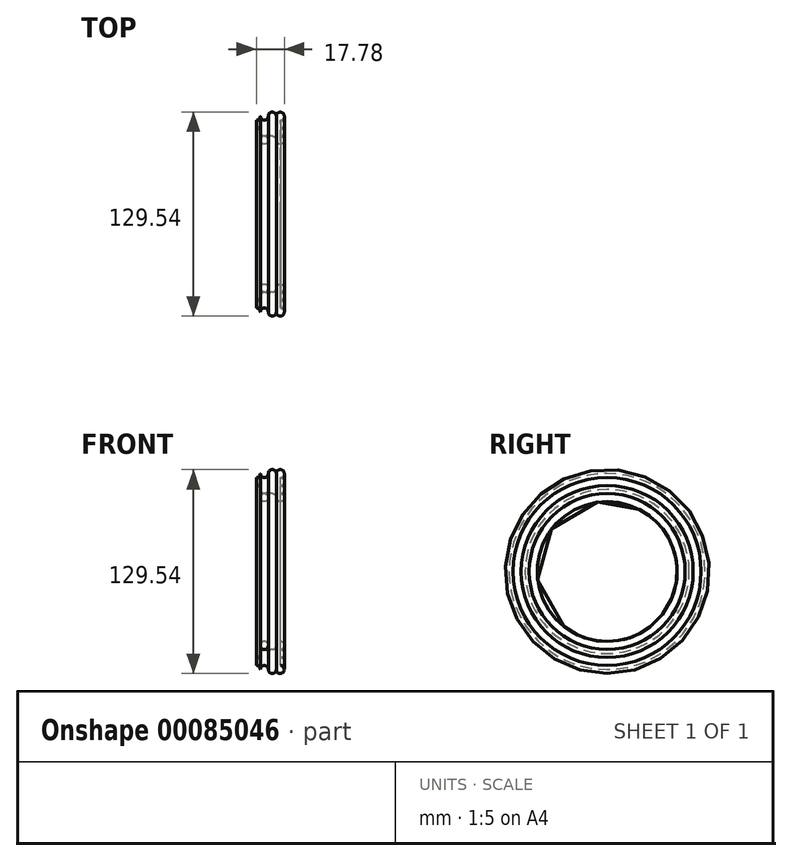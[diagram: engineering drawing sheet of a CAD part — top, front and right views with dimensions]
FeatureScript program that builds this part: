
annotation { "Feature Type Name" : "Feature", "Feature Type Description" : "" }
export const myFeature = defineFeature(function(context is Context, id is Id, definition is map)
    precondition{}
    {
        {
            var Q0;
            Q0=qCreatedBy(makeId("Front.planeOp"),FACE);
            var sketch = newSketch(context, id + "F0", { "sketchPlane" : qUnion([Q0])});
            skLineSegment(sketch, "E0", {"start": v(-20.2, 0) * mm, "end": v(26, 0) * mm, "construction": true});
            skLineSegment(sketch, "E1", {"start": v(-21.51, -21.51) * mm, "end": v(18.59, 18.59) * mm, "construction": true});
            skLineSegment(sketch, "E2", {"start": v(-19.72, 19.72) * mm, "end": v(23.47, -23.47) * mm, "construction": true});
            skCircle(sketch, "E3", {"center": v(-2.54, 2.54) * mm, "radius": 2.54 * mm});
            skCircle(sketch, "E4", {"center": v(2.54, 2.54) * mm, "radius": 2.54 * mm});
            skCircle(sketch, "E5.MirrorC", {"center": v(2.54, -2.54) * mm, "radius": 2.54 * mm});
            skCircle(sketch, "E6.MirrorC", {"center": v(-2.54, -2.54) * mm, "radius": 2.54 * mm});
            skCircle(sketch, "E7", {"center": v(7.62, 7.62) * mm, "radius": 2.54 * mm});
            skCircle(sketch, "E8", {"center": v(7.62, -7.62) * mm, "radius": 2.54 * mm});
            skCircle(sketch, "E9", {"center": v(7.62, -2.54) * mm, "radius": 2.54 * mm});
            skCircle(sketch, "E10", {"center": v(7.62, 2.54) * mm, "radius": 2.54 * mm});
            skCircle(sketch, "E11", {"center": v(2.54, 7.62) * mm, "radius": 2.54 * mm});
            skCircle(sketch, "E12.MirrorC", {"center": v(2.54, -7.62) * mm, "radius": 2.54 * mm});
            skLineSegment(sketch, "E13", {"start": v(0, -13.04) * mm, "end": v(0, 13.76) * mm, "construction": true});
            skCircle(sketch, "E14.MirrorC", {"center": v(-2.54, 7.62) * mm, "radius": 2.54 * mm});
            skCircle(sketch, "E15.MirrorC", {"center": v(-7.62, 7.62) * mm, "radius": 2.54 * mm});
            skCircle(sketch, "E16.MirrorC", {"center": v(-7.62, 2.54) * mm, "radius": 2.54 * mm});
            skCircle(sketch, "E17.MirrorC", {"center": v(-7.62, -2.54) * mm, "radius": 2.54 * mm});
            skCircle(sketch, "E18.MirrorC", {"center": v(-7.62, -7.62) * mm, "radius": 2.54 * mm});
            skCircle(sketch, "E19.MirrorC", {"center": v(-2.54, -7.62) * mm, "radius": 2.54 * mm});
            skLineSegment(sketch, "E20", {"start": v(94.82, -54.61) * mm, "end": v(-108.65, -54.61) * mm, "construction": true});
            skSolve(sketch);
        }
        {
            var Q0;
            {var subQ0=sQuery(id+"F0.wireOp",EDGE,"E8");var subQ1=makeQuery(id+"F0.imprint","INTERSECT",VERTEX,{"derivedFrom":[subQ0,sQuery(id+"F0.wireOp",EDGE,"E9")]});Q0=makeQuery(id+"F0.imprint","IMPRINT",FACE,{"disambiguationData":[TD([[makeQuery(id+"F0.imprint","IMPRINT",EDGE,{"disambiguationData":[TD([[subQ1,-1.0]])],"derivedFrom":subQ0}),1.0]])]});}
            var Q1;
            {var subQ0=sQuery(id+"F0.wireOp",EDGE,"E7");var subQ1=makeQuery(id+"F0.imprint","INTERSECT",VERTEX,{"derivedFrom":[subQ0,sQuery(id+"F0.wireOp",EDGE,"E10")]});Q1=makeQuery(id+"F0.imprint","IMPRINT",FACE,{"disambiguationData":[TD([[makeQuery(id+"F0.imprint","IMPRINT",EDGE,{"disambiguationData":[TD([[subQ1,1.0]])],"derivedFrom":subQ0}),1.0]])]});}
            var Q2;
            {var subQ0=sQuery(id+"F0.wireOp",EDGE,"E15.MirrorC");var subQ1=makeQuery(id+"F0.imprint","INTERSECT",VERTEX,{"derivedFrom":[sQuery(id+"F0.wireOp",EDGE,"E14.MirrorC"),subQ0]});Q2=makeQuery(id+"F0.imprint","IMPRINT",FACE,{"disambiguationData":[TD([[makeQuery(id+"F0.imprint","IMPRINT",EDGE,{"disambiguationData":[TD([[subQ1,-1.0]])],"derivedFrom":subQ0}),-1.0]])]});}
            var Q3;
            {var subQ0=sQuery(id+"F0.wireOp",EDGE,"E18.MirrorC");var subQ1=makeQuery(id+"F0.imprint","INTERSECT",VERTEX,{"derivedFrom":[sQuery(id+"F0.wireOp",EDGE,"E17.MirrorC"),subQ0]});Q3=makeQuery(id+"F0.imprint","IMPRINT",FACE,{"disambiguationData":[TD([[makeQuery(id+"F0.imprint","IMPRINT",EDGE,{"disambiguationData":[TD([[subQ1,-1.0]])],"derivedFrom":subQ0}),-1.0]])]});}
            var Q4;
            {var subQ0=sQuery(id+"F0.wireOp",EDGE,"E9");var subQ1=makeQuery(id+"F0.imprint","INTERSECT",VERTEX,{"derivedFrom":[subQ0,sQuery(id+"F0.wireOp",EDGE,"E10")]});Q4=makeQuery(id+"F0.imprint","IMPRINT",FACE,{"disambiguationData":[TD([[makeQuery(id+"F0.imprint","IMPRINT",EDGE,{"disambiguationData":[TD([[subQ1,-1.0]])],"derivedFrom":subQ0}),1.0]])]});}
            var Q5;
            {var subQ0=sQuery(id+"F0.wireOp",EDGE,"E5.MirrorC");var subQ1=sQuery(id+"F0.wireOp",EDGE,"E4");var subQ2=makeQuery(id+"F0.imprint","INTERSECT",VERTEX,{"derivedFrom":[subQ1,subQ0]});Q5=makeQuery(id+"F0.imprint","IMPRINT",FACE,{"disambiguationData":[TD([[makeQuery(id+"F0.imprint","IMPRINT",EDGE,{"disambiguationData":[TD([[subQ2,-1.0]])],"derivedFrom":subQ1}),-1.0]])]});}
            var Q6;
            {var subQ0=sQuery(id+"F0.wireOp",EDGE,"E12.MirrorC");var subQ1=sQuery(id+"F0.wireOp",EDGE,"E5.MirrorC");var subQ2=makeQuery(id+"F0.imprint","INTERSECT",VERTEX,{"derivedFrom":[subQ1,subQ0]});Q6=makeQuery(id+"F0.imprint","IMPRINT",FACE,{"disambiguationData":[TD([[makeQuery(id+"F0.imprint","IMPRINT",EDGE,{"disambiguationData":[TD([[subQ2,1.0]])],"derivedFrom":subQ1}),1.0]])]});}
            var Q7;
            {var subQ0=sQuery(id+"F0.wireOp",EDGE,"E10");var subQ1=makeQuery(id+"F0.imprint","INTERSECT",VERTEX,{"derivedFrom":[sQuery(id+"F0.wireOp",EDGE,"E7"),subQ0]});Q7=makeQuery(id+"F0.imprint","IMPRINT",FACE,{"disambiguationData":[TD([[makeQuery(id+"F0.imprint","IMPRINT",EDGE,{"disambiguationData":[TD([[subQ1,-1.0]])],"derivedFrom":subQ0}),1.0]])]});}
            var Q8;
            {var subQ0=sQuery(id+"F0.wireOp",EDGE,"E11");var subQ1=makeQuery(id+"F0.imprint","INTERSECT",VERTEX,{"derivedFrom":[sQuery(id+"F0.wireOp",EDGE,"E7"),subQ0]});Q8=makeQuery(id+"F0.imprint","IMPRINT",FACE,{"disambiguationData":[TD([[makeQuery(id+"F0.imprint","IMPRINT",EDGE,{"disambiguationData":[TD([[subQ1,-1.0]])],"derivedFrom":subQ0}),1.0]])]});}
            var Q9;
            {var subQ0=sQuery(id+"F0.wireOp",EDGE,"E17.MirrorC");var subQ1=sQuery(id+"F0.wireOp",EDGE,"E6.MirrorC");var subQ2=makeQuery(id+"F0.imprint","INTERSECT",VERTEX,{"derivedFrom":[subQ1,subQ0]});Q9=makeQuery(id+"F0.imprint","IMPRINT",FACE,{"disambiguationData":[TD([[makeQuery(id+"F0.imprint","IMPRINT",EDGE,{"disambiguationData":[TD([[subQ2,1.0]])],"derivedFrom":subQ1}),1.0]])]});}
            var Q10;
            {var subQ0=sQuery(id+"F0.wireOp",EDGE,"E12.MirrorC");var subQ1=makeQuery(id+"F0.imprint","INTERSECT",VERTEX,{"derivedFrom":[sQuery(id+"F0.wireOp",EDGE,"E8"),subQ0]});Q10=makeQuery(id+"F0.imprint","IMPRINT",FACE,{"disambiguationData":[TD([[makeQuery(id+"F0.imprint","IMPRINT",EDGE,{"disambiguationData":[TD([[subQ1,-1.0]])],"derivedFrom":subQ0}),-1.0]])]});}
            var Q11;
            {var subQ0=sQuery(id+"F0.wireOp",EDGE,"E14.MirrorC");var subQ1=makeQuery(id+"F0.imprint","INTERSECT",VERTEX,{"derivedFrom":[sQuery(id+"F0.wireOp",EDGE,"E11"),subQ0]});Q11=makeQuery(id+"F0.imprint","IMPRINT",FACE,{"disambiguationData":[TD([[makeQuery(id+"F0.imprint","IMPRINT",EDGE,{"disambiguationData":[TD([[subQ1,1.0]])],"derivedFrom":subQ0}),-1.0]])]});}
            var Q12;
            {var subQ0=sQuery(id+"F0.wireOp",EDGE,"E16.MirrorC");var subQ1=makeQuery(id+"F0.imprint","INTERSECT",VERTEX,{"derivedFrom":[sQuery(id+"F0.wireOp",EDGE,"E15.MirrorC"),subQ0]});Q12=makeQuery(id+"F0.imprint","IMPRINT",FACE,{"disambiguationData":[TD([[makeQuery(id+"F0.imprint","IMPRINT",EDGE,{"disambiguationData":[TD([[subQ1,-1.0]])],"derivedFrom":subQ0}),-1.0]])]});}
            var Q13;
            {var subQ0=sQuery(id+"F0.wireOp",EDGE,"E17.MirrorC");var subQ1=makeQuery(id+"F0.imprint","INTERSECT",VERTEX,{"derivedFrom":[sQuery(id+"F0.wireOp",EDGE,"E16.MirrorC"),subQ0]});Q13=makeQuery(id+"F0.imprint","IMPRINT",FACE,{"disambiguationData":[TD([[makeQuery(id+"F0.imprint","IMPRINT",EDGE,{"disambiguationData":[TD([[subQ1,-1.0]])],"derivedFrom":subQ0}),-1.0]])]});}
            var Q14;
            {var subQ0=sQuery(id+"F0.wireOp",EDGE,"E19.MirrorC");var subQ1=makeQuery(id+"F0.imprint","INTERSECT",VERTEX,{"derivedFrom":[sQuery(id+"F0.wireOp",EDGE,"E12.MirrorC"),subQ0]});Q14=makeQuery(id+"F0.imprint","IMPRINT",FACE,{"disambiguationData":[TD([[makeQuery(id+"F0.imprint","IMPRINT",EDGE,{"disambiguationData":[TD([[subQ1,1.0]])],"derivedFrom":subQ0}),1.0]])]});}
            var Q15;
            {var subQ0=sQuery(id+"F0.wireOp",EDGE,"E11");var subQ1=sQuery(id+"F0.wireOp",EDGE,"E4");var subQ2=makeQuery(id+"F0.imprint","INTERSECT",VERTEX,{"derivedFrom":[subQ1,subQ0]});Q15=makeQuery(id+"F0.imprint","IMPRINT",FACE,{"disambiguationData":[TD([[makeQuery(id+"F0.imprint","IMPRINT",EDGE,{"disambiguationData":[TD([[subQ2,1.0]])],"derivedFrom":subQ1}),-1.0]])]});}
            var Q16;
            {var subQ0=sQuery(id+"F0.wireOp",EDGE,"E6.MirrorC");var subQ1=sQuery(id+"F0.wireOp",EDGE,"E5.MirrorC");var subQ2=makeQuery(id+"F0.imprint","INTERSECT",VERTEX,{"derivedFrom":[subQ1,subQ0]});Q16=makeQuery(id+"F0.imprint","IMPRINT",FACE,{"disambiguationData":[TD([[makeQuery(id+"F0.imprint","IMPRINT",EDGE,{"disambiguationData":[TD([[subQ2,1.0]])],"derivedFrom":subQ1}),1.0]])]});}
            var Q17;
            {var subQ0=sQuery(id+"F0.wireOp",EDGE,"E16.MirrorC");var subQ1=sQuery(id+"F0.wireOp",EDGE,"E3");var subQ2=makeQuery(id+"F0.imprint","INTERSECT",VERTEX,{"derivedFrom":[subQ1,subQ0]});Q17=makeQuery(id+"F0.imprint","IMPRINT",FACE,{"disambiguationData":[TD([[makeQuery(id+"F0.imprint","IMPRINT",EDGE,{"disambiguationData":[TD([[subQ2,-1.0]])],"derivedFrom":subQ1}),-1.0]])]});}
            var Q18;
            {var subQ0=sQuery(id+"F0.wireOp",EDGE,"E14.MirrorC");var subQ1=sQuery(id+"F0.wireOp",EDGE,"E3");var subQ2=makeQuery(id+"F0.imprint","INTERSECT",VERTEX,{"derivedFrom":[subQ1,subQ0]});Q18=makeQuery(id+"F0.imprint","IMPRINT",FACE,{"disambiguationData":[TD([[makeQuery(id+"F0.imprint","IMPRINT",EDGE,{"disambiguationData":[TD([[subQ2,1.0]])],"derivedFrom":subQ1}),-1.0]])]});}
            var Q19;
            {var subQ0=sQuery(id+"F0.wireOp",EDGE,"E5.MirrorC");var subQ1=makeQuery(id+"F0.imprint","INTERSECT",VERTEX,{"derivedFrom":[subQ0,sQuery(id+"F0.wireOp",EDGE,"E6.MirrorC")]});Q19=makeQuery(id+"F0.imprint","IMPRINT",FACE,{"disambiguationData":[TD([[makeQuery(id+"F0.imprint","IMPRINT",EDGE,{"disambiguationData":[TD([[subQ1,1.0]])],"derivedFrom":subQ0}),-1.0]])]});}
            var Q20;
            {var subQ0=sQuery(id+"F0.wireOp",EDGE,"E16.MirrorC");var subQ1=sQuery(id+"F0.wireOp",EDGE,"E3");var subQ2=makeQuery(id+"F0.imprint","INTERSECT",VERTEX,{"derivedFrom":[subQ1,subQ0]});Q20=makeQuery(id+"F0.imprint","IMPRINT",FACE,{"disambiguationData":[TD([[makeQuery(id+"F0.imprint","IMPRINT",EDGE,{"disambiguationData":[TD([[subQ2,1.0]])],"derivedFrom":subQ1}),-1.0]])]});}
            var Q21;
            {var subQ0=sQuery(id+"F0.wireOp",EDGE,"E6.MirrorC");var subQ1=sQuery(id+"F0.wireOp",EDGE,"E3");var subQ2=makeQuery(id+"F0.imprint","INTERSECT",VERTEX,{"derivedFrom":[subQ1,subQ0]});Q21=makeQuery(id+"F0.imprint","IMPRINT",FACE,{"disambiguationData":[TD([[makeQuery(id+"F0.imprint","IMPRINT",EDGE,{"disambiguationData":[TD([[subQ2,-1.0]])],"derivedFrom":subQ1}),-1.0]])]});}
            var Q22;
            {var subQ0=sQuery(id+"F0.wireOp",EDGE,"E3");var subQ1=makeQuery(id+"F0.imprint","INTERSECT",VERTEX,{"derivedFrom":[subQ0,sQuery(id+"F0.wireOp",EDGE,"E16.MirrorC")]});Q22=makeQuery(id+"F0.imprint","IMPRINT",FACE,{"disambiguationData":[TD([[makeQuery(id+"F0.imprint","IMPRINT",EDGE,{"disambiguationData":[TD([[subQ1,1.0]])],"derivedFrom":subQ0}),1.0]])]});}
            var Q23;
            {var subQ0=sQuery(id+"F0.wireOp",EDGE,"E4");var subQ1=makeQuery(id+"F0.imprint","INTERSECT",VERTEX,{"derivedFrom":[sQuery(id+"F0.wireOp",EDGE,"E3"),subQ0]});Q23=makeQuery(id+"F0.imprint","IMPRINT",FACE,{"disambiguationData":[TD([[makeQuery(id+"F0.imprint","IMPRINT",EDGE,{"disambiguationData":[TD([[subQ1,1.0]])],"derivedFrom":subQ0}),1.0]])]});}
            var Q24;
            {var subQ0=sQuery(id+"F0.wireOp",EDGE,"E6.MirrorC");var subQ1=makeQuery(id+"F0.imprint","INTERSECT",VERTEX,{"derivedFrom":[subQ0,sQuery(id+"F0.wireOp",EDGE,"E17.MirrorC")]});Q24=makeQuery(id+"F0.imprint","IMPRINT",FACE,{"disambiguationData":[TD([[makeQuery(id+"F0.imprint","IMPRINT",EDGE,{"disambiguationData":[TD([[subQ1,1.0]])],"derivedFrom":subQ0}),-1.0]])]});}
            var Q25;
            Q25=sQuery(id+"F0.wireOp",EDGE,"E20");
            revolve(context, id + "F1", {"entities" : qUnion([Q0, Q1, Q2, Q3, Q4, Q5, Q6, Q7, Q8, Q9, Q10, Q11, Q12, Q13, Q14, Q15, Q16, Q17, Q18, Q19, Q20, Q21, Q22, Q23, Q24]), "axis" : qUnion([Q25]), "revolveType" : RevolveType.FULL});
        }
    });
